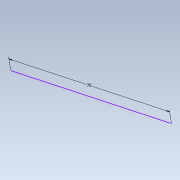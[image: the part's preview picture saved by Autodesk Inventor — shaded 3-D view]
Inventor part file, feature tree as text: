
AUTODESK INVENTOR PART (.ipt)
format: ipt  version: 2021 (Build 250183000, 183)  size: 64,512 bytes
history: native  units: mm
features: sketch x1
ambient origin geometry x8: Origin, YZ Plane, XZ Plane, XY Plane, X Axis, Y Axis, Z Axis, Center Point
feature tree (1):
  sketch  "Sketch1"  dims[d0=75.0mm]
